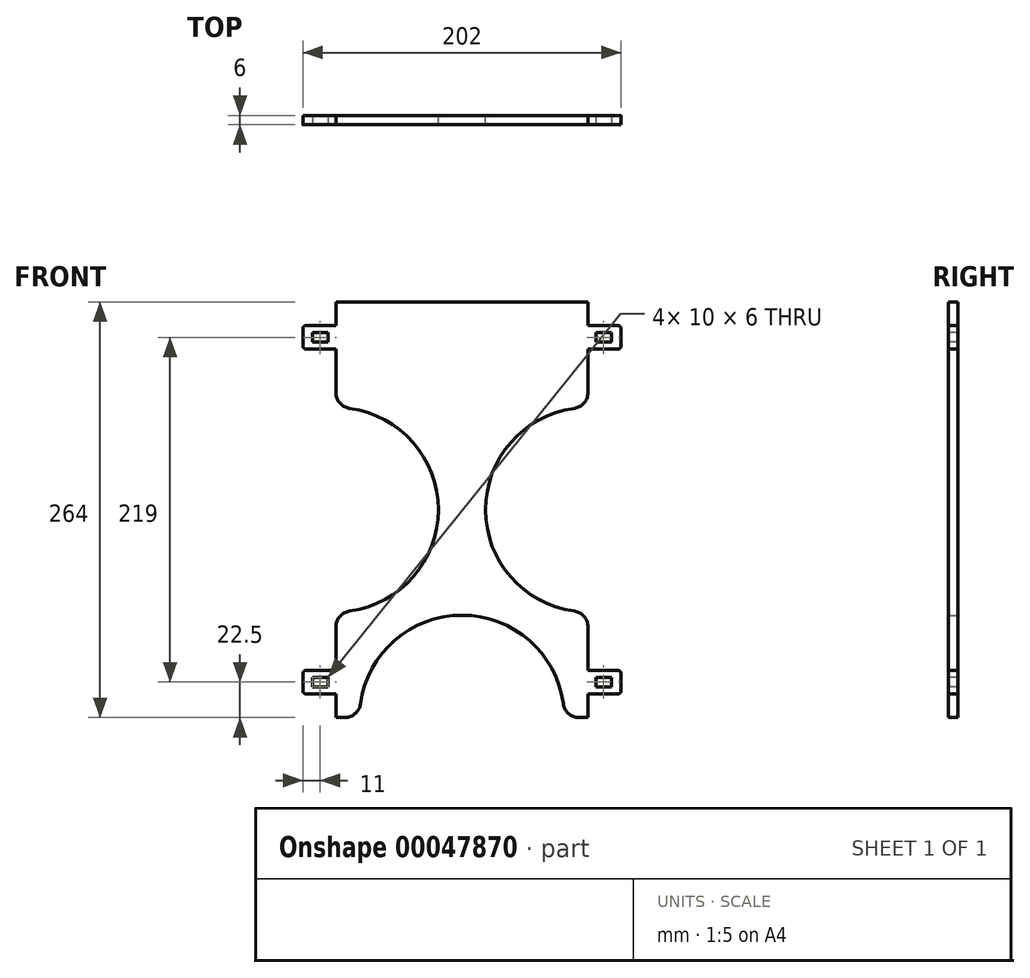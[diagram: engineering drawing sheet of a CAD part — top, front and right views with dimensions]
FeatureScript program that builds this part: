
annotation { "Feature Type Name" : "Feature", "Feature Type Description" : "" }
export const myFeature = defineFeature(function(context is Context, id is Id, definition is map)
    precondition{}
    {
        {
            var Q0;
            Q0=qCreatedBy(makeId("Front.planeOp"),FACE);
            var sketch = newSketch(context, id + "F0", { "sketchPlane" : qUnion([Q0])});
            skLineSegment(sketch, "E0.rect.bottom", {"start": v(-80, 132) * mm, "end": v(80, 132) * mm});
            skLineSegment(sketch, "E0.rect.top", {"start": v(-80, -132) * mm, "end": v(-74.33, -132) * mm});
            skLineSegment(sketch, "E0.rect.left", {"start": v(-80, 132) * mm, "end": v(-80, 74.33) * mm});
            skLineSegment(sketch, "E0.rect.right", {"start": v(80, 132) * mm, "end": v(80, 74.33) * mm});
            skPoint(sketch, "E0.rect.middle", {"position": v(0, 0) * mm});
            skLineSegment(sketch, "E1", {"start": v(-80, 117) * mm, "end": v(80, 117) * mm, "construction": true});
            skLineSegment(sketch, "E2.bottom", {"start": v(80, 117) * mm, "end": v(99, 117) * mm});
            skLineSegment(sketch, "E2.top", {"start": v(80, 102) * mm, "end": v(99, 102) * mm});
            skLineSegment(sketch, "E2.left", {"start": v(80, 117) * mm, "end": v(80, 102) * mm});
            skLineSegment(sketch, "E2.right", {"start": v(101, 115) * mm, "end": v(101, 104) * mm});
            skLineSegment(sketch, "E3.MirrorCS", {"start": v(-80, 102) * mm, "end": v(-99, 102) * mm});
            skLineSegment(sketch, "E4.MirrorCS", {"start": v(-101, 115) * mm, "end": v(-101, 104) * mm});
            skLineSegment(sketch, "E5.MirrorCS", {"start": v(-80, 117) * mm, "end": v(-99, 117) * mm});
            skLineSegment(sketch, "E6.MirrorCS", {"start": v(80, -102) * mm, "end": v(99, -102) * mm});
            skLineSegment(sketch, "E7.MirrorCS", {"start": v(101, -115) * mm, "end": v(101, -104) * mm});
            skLineSegment(sketch, "E8.MirrorCS", {"start": v(80, -117) * mm, "end": v(99, -117) * mm});
            skLineSegment(sketch, "E9.MirrorCS", {"start": v(-80, -102) * mm, "end": v(-99, -102) * mm});
            skLineSegment(sketch, "E10.MirrorCS", {"start": v(-101, -115) * mm, "end": v(-101, -104) * mm});
            skLineSegment(sketch, "E11.MirrorCS", {"start": v(-80, -117) * mm, "end": v(-99, -117) * mm});
            skArc(sketch, "E12", {"start": v(64.42, -123.33) * mm, "mid": v(0, -67) * mm, "end": v(-64.42, -123.33) * mm});
            skArc(sketch, "E13", {"start": v(71.33, 64.42) * mm, "mid": v(15, 0) * mm, "end": v(71.33, -64.42) * mm});
            skArc(sketch, "E14.MirrorC", {"start": v(-71.33, 64.42) * mm, "mid": v(-15, 0) * mm, "end": v(-71.33, -64.42) * mm});
            skLineSegment(sketch, "E15.trimOffspring", {"start": v(-80, -74.33) * mm, "end": v(-80, -132) * mm});
            skLineSegment(sketch, "E16.trimOffspring", {"start": v(80, -74.33) * mm, "end": v(80, -132) * mm});
            skLineSegment(sketch, "E17.trimOffspring", {"start": v(74.33, -132) * mm, "end": v(80, -132) * mm});
            skPoint(sketch, "E18.visualSharp", {"position": v(-101, 117) * mm});
            skArc(sketch, "E18.filletArc", {"start": v(-99, 117) * mm, "mid": v(-100.41, 116.41) * mm, "end": v(-101, 115) * mm});
            skPoint(sketch, "E19.visualSharp", {"position": v(-101, 102) * mm});
            skArc(sketch, "E19.filletArc", {"start": v(-101, 104) * mm, "mid": v(-100.41, 102.59) * mm, "end": v(-99, 102) * mm});
            skPoint(sketch, "E20.visualSharp", {"position": v(101, 117) * mm});
            skArc(sketch, "E20.filletArc", {"start": v(101, 115) * mm, "mid": v(100.41, 116.41) * mm, "end": v(99, 117) * mm});
            skPoint(sketch, "E21.visualSharp", {"position": v(101, 102) * mm});
            skArc(sketch, "E21.filletArc", {"start": v(99, 102) * mm, "mid": v(100.41, 102.59) * mm, "end": v(101, 104) * mm});
            skPoint(sketch, "E22.visualSharp", {"position": v(101, -102) * mm});
            skArc(sketch, "E22.filletArc", {"start": v(101, -104) * mm, "mid": v(100.41, -102.59) * mm, "end": v(99, -102) * mm});
            skPoint(sketch, "E23.visualSharp", {"position": v(101, -117) * mm});
            skArc(sketch, "E23.filletArc", {"start": v(99, -117) * mm, "mid": v(100.41, -116.41) * mm, "end": v(101, -115) * mm});
            skPoint(sketch, "E24.visualSharp", {"position": v(-101, -102) * mm});
            skArc(sketch, "E24.filletArc", {"start": v(-99, -102) * mm, "mid": v(-100.41, -102.59) * mm, "end": v(-101, -104) * mm});
            skPoint(sketch, "E25.visualSharp", {"position": v(-101, -117) * mm});
            skArc(sketch, "E25.filletArc", {"start": v(-101, -115) * mm, "mid": v(-100.41, -116.41) * mm, "end": v(-99, -117) * mm});
            skPoint(sketch, "E26.visualSharp", {"position": v(-80, 65) * mm});
            skArc(sketch, "E26.filletArc", {"start": v(-80, 74.33) * mm, "mid": v(-77.53, 67.75) * mm, "end": v(-71.33, 64.42) * mm});
            skPoint(sketch, "E27.visualSharp", {"position": v(-80, -65) * mm});
            skArc(sketch, "E27.filletArc", {"start": v(-71.33, -64.42) * mm, "mid": v(-77.53, -67.75) * mm, "end": v(-80, -74.33) * mm});
            skPoint(sketch, "E28.visualSharp", {"position": v(80, -65) * mm});
            skArc(sketch, "E28.filletArc", {"start": v(80, -74.33) * mm, "mid": v(77.53, -67.75) * mm, "end": v(71.33, -64.42) * mm});
            skPoint(sketch, "E29.visualSharp", {"position": v(80, 65) * mm});
            skArc(sketch, "E29.filletArc", {"start": v(71.33, 64.42) * mm, "mid": v(77.53, 67.75) * mm, "end": v(80, 74.33) * mm});
            skPoint(sketch, "E30.visualSharp", {"position": v(65, -132) * mm});
            skArc(sketch, "E30.filletArc", {"start": v(64.42, -123.33) * mm, "mid": v(67.75, -129.53) * mm, "end": v(74.33, -132) * mm});
            skPoint(sketch, "E31.visualSharp", {"position": v(-65, -132) * mm});
            skArc(sketch, "E31.filletArc", {"start": v(-74.33, -132) * mm, "mid": v(-67.75, -129.53) * mm, "end": v(-64.42, -123.33) * mm});
            skSolve(sketch);
        }
        {
            var Q0;
            Q0 = qSketchRegion(id + "F0", true);
            extrude(context, id + "F1", {"entities" : qUnion([Q0]), "depth" : 6 * mm});
        }
        {
            var Q0;
            Q0=makeQuery(id+"F1.opExtrude","CAP_FACE",FACE,{"disambiguationData":[OSD([sQuery(id+"F0.wireOp",EDGE,"E0.rect.bottom"),sQuery(id+"F0.wireOp",EDGE,"E0.rect.top"),sQuery(id+"F0.wireOp",EDGE,"E0.rect.left"),sQuery(id+"F0.wireOp",EDGE,"E0.rect.right"),sQuery(id+"F0.wireOp",EDGE,"E2.bottom"),sQuery(id+"F0.wireOp",EDGE,"E2.top"),sQuery(id+"F0.wireOp",EDGE,"E2.right"),sQuery(id+"F0.wireOp",EDGE,"E3.MirrorCS"),sQuery(id+"F0.wireOp",EDGE,"E4.MirrorCS"),sQuery(id+"F0.wireOp",EDGE,"E5.MirrorCS"),sQuery(id+"F0.wireOp",EDGE,"E6.MirrorCS"),sQuery(id+"F0.wireOp",EDGE,"E7.MirrorCS"),sQuery(id+"F0.wireOp",EDGE,"E8.MirrorCS"),sQuery(id+"F0.wireOp",EDGE,"E9.MirrorCS"),sQuery(id+"F0.wireOp",EDGE,"E10.MirrorCS"),sQuery(id+"F0.wireOp",EDGE,"E11.MirrorCS"),sQuery(id+"F0.wireOp",EDGE,"E12"),sQuery(id+"F0.wireOp",EDGE,"E13"),sQuery(id+"F0.wireOp",EDGE,"E14.MirrorC"),sQuery(id+"F0.wireOp",EDGE,"E15.trimOffspring"),sQuery(id+"F0.wireOp",EDGE,"E16.trimOffspring"),sQuery(id+"F0.wireOp",EDGE,"E17.trimOffspring"),sQuery(id+"F0.wireOp",EDGE,"E18.filletArc"),sQuery(id+"F0.wireOp",EDGE,"E19.filletArc"),sQuery(id+"F0.wireOp",EDGE,"E20.filletArc"),sQuery(id+"F0.wireOp",EDGE,"E21.filletArc"),sQuery(id+"F0.wireOp",EDGE,"E22.filletArc"),sQuery(id+"F0.wireOp",EDGE,"E23.filletArc"),sQuery(id+"F0.wireOp",EDGE,"E24.filletArc"),sQuery(id+"F0.wireOp",EDGE,"E25.filletArc"),sQuery(id+"F0.wireOp",EDGE,"E26.filletArc"),sQuery(id+"F0.wireOp",EDGE,"E27.filletArc"),sQuery(id+"F0.wireOp",EDGE,"E28.filletArc"),sQuery(id+"F0.wireOp",EDGE,"E29.filletArc"),sQuery(id+"F0.wireOp",EDGE,"E30.filletArc"),sQuery(id+"F0.wireOp",EDGE,"E31.filletArc")])],"isStart":false});
            var sketch = newSketch(context, id + "F2", { "sketchPlane" : qUnion([Q0])});
            skLineSegment(sketch, "E32.bottom", {"start": v(-95, 112.5) * mm, "end": v(-85, 112.5) * mm});
            skLineSegment(sketch, "E32.top", {"start": v(-95, 106.5) * mm, "end": v(-85, 106.5) * mm});
            skLineSegment(sketch, "E32.left", {"start": v(-95, 112.5) * mm, "end": v(-95, 106.5) * mm});
            skLineSegment(sketch, "E32.right", {"start": v(-85, 112.5) * mm, "end": v(-85, 106.5) * mm});
            skLineSegment(sketch, "E33", {"start": v(-80, 117) * mm, "end": v(-80, 102) * mm, "construction": true});
            skLineSegment(sketch, "E34", {"start": v(-80, 109.5) * mm, "end": v(-98.66, 109.5) * mm, "construction": true});
            skPoint(sketch, "E35", {"position": v(-85, 109.5) * mm});
            skLineSegment(sketch, "E36.MirrorCS", {"start": v(95, 112.5) * mm, "end": v(85, 112.5) * mm});
            skLineSegment(sketch, "E37.MirrorCS", {"start": v(95, 112.5) * mm, "end": v(95, 106.5) * mm});
            skLineSegment(sketch, "E38.MirrorCS", {"start": v(95, 106.5) * mm, "end": v(85, 106.5) * mm});
            skLineSegment(sketch, "E39.MirrorCS", {"start": v(85, 112.5) * mm, "end": v(85, 106.5) * mm});
            skLineSegment(sketch, "E40.MirrorCS", {"start": v(-95, -106.5) * mm, "end": v(-85, -106.5) * mm});
            skLineSegment(sketch, "E41.MirrorCS", {"start": v(-95, -112.5) * mm, "end": v(-95, -106.5) * mm});
            skLineSegment(sketch, "E42.MirrorCS", {"start": v(-95, -112.5) * mm, "end": v(-85, -112.5) * mm});
            skLineSegment(sketch, "E43.MirrorCS", {"start": v(-85, -112.5) * mm, "end": v(-85, -106.5) * mm});
            skLineSegment(sketch, "E44.MirrorCS", {"start": v(95, -112.5) * mm, "end": v(85, -112.5) * mm});
            skLineSegment(sketch, "E45.MirrorCS", {"start": v(85, -112.5) * mm, "end": v(85, -106.5) * mm});
            skLineSegment(sketch, "E46.MirrorCS", {"start": v(95, -106.5) * mm, "end": v(85, -106.5) * mm});
            skLineSegment(sketch, "E47.MirrorCS", {"start": v(95, -112.5) * mm, "end": v(95, -106.5) * mm});
            skSolve(sketch);
        }
        {
            var Q0;
            Q0 = qSketchRegion(id + "F2", true);
            extrude(context, id + "F3", {"entities" : qUnion([Q0]), "operationType" : NewBodyOperationType.REMOVE, "oppositeDirection" : true, "depth" : 25 * mm});
        }
    });
